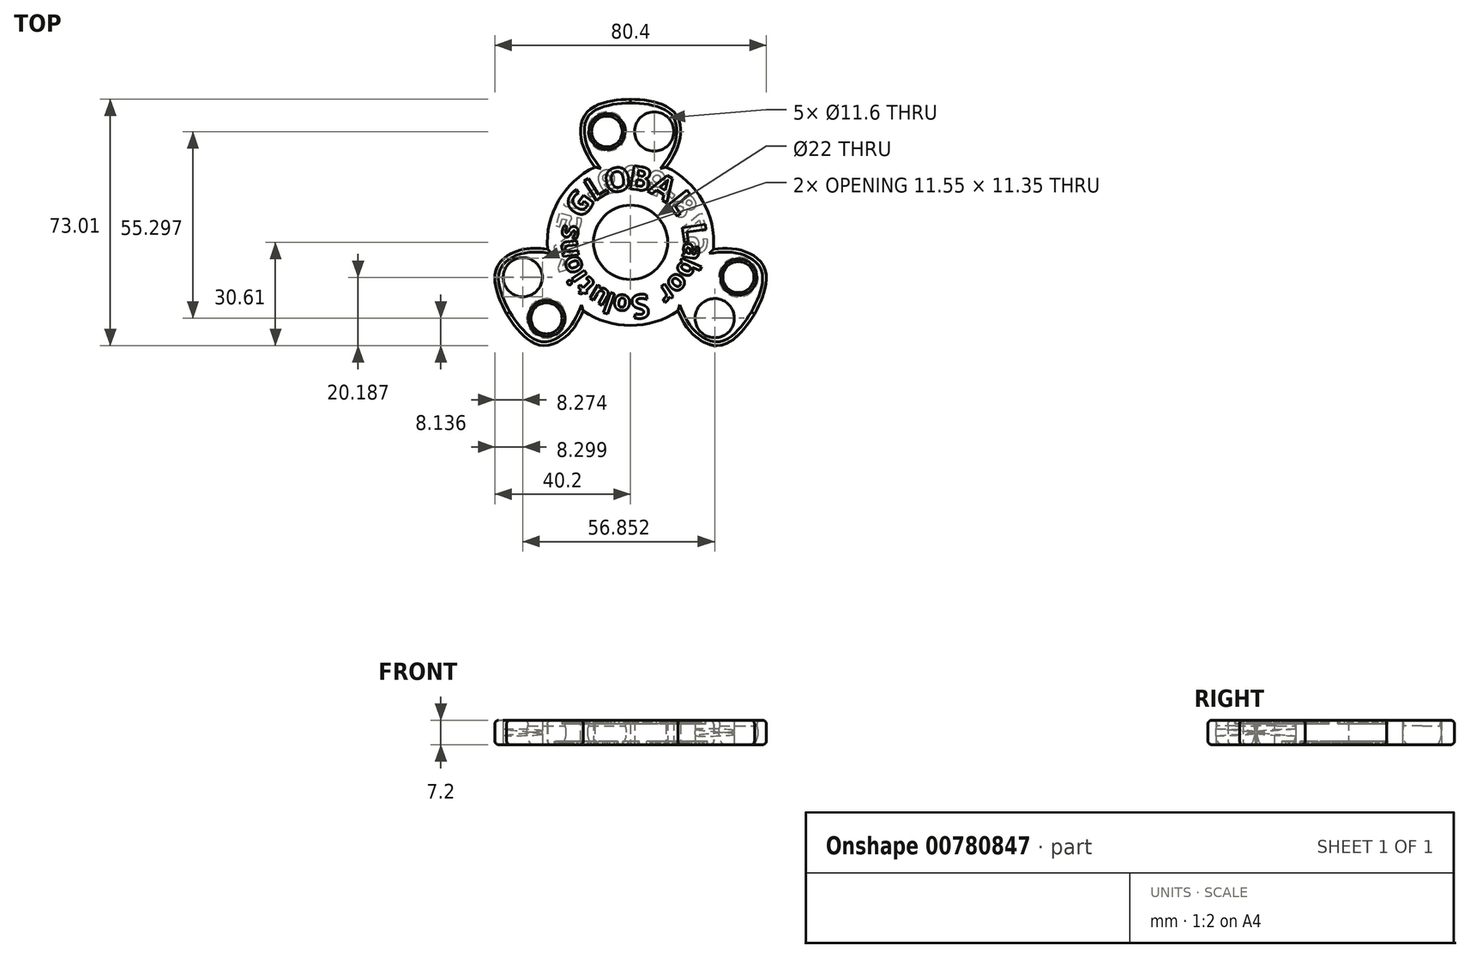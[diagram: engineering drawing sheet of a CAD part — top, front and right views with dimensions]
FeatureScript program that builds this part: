
annotation { "Feature Type Name" : "Feature", "Feature Type Description" : "" }
export const myFeature = defineFeature(function(context is Context, id is Id, definition is map)
    precondition{}
    {
        {
            var Q0;
            Q0=qCreatedBy(makeId("Top.planeOp"),FACE);
            var sketch = newSketch(context, id + "F0", { "sketchPlane" : qUnion([Q0])});
            skCircle(sketch, "E0", {"center": v(0, 0) * mm, "radius": 11 * mm});
            skLineSegment(sketch, "E1", {"start": v(-60.62, 35) * mm, "end": v(57.4, -33.14) * mm, "construction": true});
            skLineSegment(sketch, "E2.MirrorCS", {"start": v(-60.62, -35) * mm, "end": v(57.4, 33.14) * mm, "construction": true});
            skLineSegment(sketch, "E3", {"start": v(-61.07, 42.4) * mm, "end": v(58.93, 42.4) * mm, "construction": true});
            skFitSpline(sketch, "E4", {"points": [v(-10.53, 22.28) * mm, v(-14.78, 33.34) * mm, v(0, 42.4) * mm], "startDerivative": vector(-20.82, 27.32) * mm, "endDerivative": vector(68.91, 1.84) * mm});
            skCircle(sketch, "E5", {"center": v(-7, 32.82) * mm, "radius": 5.8 * mm});
            skFitSpline(sketch, "E6.MirrorCS", {"points": [v(10.53, 22.28) * mm, v(14.78, 33.34) * mm, v(0, 42.4) * mm], "startDerivative": vector(20.82, 27.32) * mm, "endDerivative": vector(-68.91, 1.84) * mm});
            skCircle(sketch, "E7.MirrorC", {"center": v(7, 32.82) * mm, "radius": 5.8 * mm});
            skFitSpline(sketch, "E8.MirrorCS", {"points": [v(24.56, -2.02) * mm, v(36.26, -3.87) * mm, v(36.72, -21.2) * mm], "startDerivative": vector(34.07, 4.37) * mm, "endDerivative": vector(-32.86, -60.6) * mm});
            skFitSpline(sketch, "E9.MirrorCS", {"points": [v(14.03, -20.26) * mm, v(21.48, -29.47) * mm, v(36.72, -21.2) * mm], "startDerivative": vector(13.25, -31.7) * mm, "endDerivative": vector(36.05, 58.76) * mm});
            skCircle(sketch, "E10.MirrorC", {"center": v(24.93, -22.47) * mm, "radius": 5.8 * mm});
            skCircle(sketch, "E11.MirrorC", {"center": v(31.93, -10.35) * mm, "radius": 5.8 * mm});
            skFitSpline(sketch, "E12.MirrorCS", {"points": [v(-14.03, -20.26) * mm, v(-21.48, -29.47) * mm, v(-36.72, -21.2) * mm], "startDerivative": vector(-13.25, -31.7) * mm, "endDerivative": vector(-36.05, 58.76) * mm});
            skFitSpline(sketch, "E13.MirrorCS", {"points": [v(-24.56, -2.02) * mm, v(-36.26, -3.87) * mm, v(-36.72, -21.2) * mm], "startDerivative": vector(-34.07, 4.37) * mm, "endDerivative": vector(32.86, -60.6) * mm});
            skCircle(sketch, "E14.MirrorC", {"center": v(-31.93, -10.35) * mm, "radius": 5.8 * mm});
            skCircle(sketch, "E15.MirrorC", {"center": v(-24.93, -22.47) * mm, "radius": 5.8 * mm});
            skArc(sketch, "E16", {"start": v(-14.03, -20.26) * mm, "mid": v(0, -24.65) * mm, "end": v(14.03, -20.26) * mm});
            skArc(sketch, "E17.trimOffspring", {"start": v(-10.53, 22.28) * mm, "mid": v(-21.34, 12.32) * mm, "end": v(-24.56, -2.02) * mm});
            skArc(sketch, "E18.trimOffspring", {"start": v(24.56, -2.02) * mm, "mid": v(21.34, 12.32) * mm, "end": v(10.53, 22.28) * mm});
            skSolve(sketch);
        }
        {
            var Q0;
            {var subQ0=sQuery(id+"F0.wireOp",EDGE,"c7664de7-02b4-4db1-8378-9aed48db6bc2");Q0=makeQuery(id+"F0.imprint","IMPRINT",FACE,{"disambiguationData":[TD([[makeQuery(id+"F0.imprint","IMPRINT",EDGE,{"derivedFrom":subQ0}),-1.0]])]});}
            var Q1;
            Q1=makeQuery(id+"F0.imprint","IMPRINT",FACE,{"disambiguationData":[TD([[makeQuery(id+"F0.imprint","IMPRINT",EDGE,{"derivedFrom":sQuery(id+"F0.wireOp",EDGE,"E5")}),1.0]])]});
            var Q2;
            Q2=makeQuery(id+"F0.imprint","IMPRINT",FACE,{"disambiguationData":[TD([[makeQuery(id+"F0.imprint","IMPRINT",EDGE,{"derivedFrom":sQuery(id+"F0.wireOp",EDGE,"E7.MirrorC")}),-1.0]])]});
            var Q3;
            {var subQ0=sQuery(id+"F0.wireOp",EDGE,"b568a12d-a18f-46d6-a3cd-37dfae46e10a0.MirrorCS");Q3=makeQuery(id+"F0.imprint","IMPRINT",FACE,{"disambiguationData":[TD([[makeQuery(id+"F0.imprint","IMPRINT",EDGE,{"derivedFrom":subQ0}),1.0]])]});}
            var Q4;
            Q4=makeQuery(id+"F0.imprint","IMPRINT",FACE,{"disambiguationData":[TD([[makeQuery(id+"F0.imprint","IMPRINT",EDGE,{"derivedFrom":sQuery(id+"F0.wireOp",EDGE,"E8.MirrorCS")}),-1.0]])]});
            var Q5;
            Q5=makeQuery(id+"F0.imprint","IMPRINT",FACE,{"disambiguationData":[TD([[makeQuery(id+"F0.imprint","IMPRINT",EDGE,{"derivedFrom":sQuery(id+"F0.wireOp",EDGE,"E0")}),-1.0]])]});
            var Q6;
            Q6=makeQuery(id+"F0.imprint","IMPRINT",FACE,{"disambiguationData":[TD([[makeQuery(id+"F0.imprint","IMPRINT",EDGE,{"derivedFrom":sQuery(id+"F0.wireOp",EDGE,"E15.MirrorC")}),1.0]])]});
            var Q7;
            Q7=makeQuery(id+"F0.imprint","IMPRINT",FACE,{"disambiguationData":[TD([[makeQuery(id+"F0.imprint","IMPRINT",EDGE,{"derivedFrom":sQuery(id+"F0.wireOp",EDGE,"E14.MirrorC")}),-1.0]])]});
            var Q8;
            Q8=makeQuery(id+"F0.imprint","IMPRINT",FACE,{"disambiguationData":[TD([[makeQuery(id+"F0.imprint","IMPRINT",EDGE,{"derivedFrom":sQuery(id+"F0.wireOp",EDGE,"E10.MirrorC")}),-1.0]])]});
            var Q9;
            Q9=makeQuery(id+"F0.imprint","IMPRINT",FACE,{"disambiguationData":[TD([[makeQuery(id+"F0.imprint","IMPRINT",EDGE,{"derivedFrom":sQuery(id+"F0.wireOp",EDGE,"E11.MirrorC")}),1.0]])]});
            var Q10;
            {var subQ1=sQuery(id+"F0.wireOp",EDGE,"E12.MirrorCS");Q10=makeQuery(id+"F0.imprint","IMPRINT",FACE,{"disambiguationData":[TD([[makeQuery(id+"F0.imprint","IMPRINT",EDGE,{"derivedFrom":subQ1}),-1.0]])]});}
            var Q11;
            {var subQ1=sQuery(id+"F0.wireOp",EDGE,"E4");Q11=makeQuery(id+"F0.imprint","IMPRINT",FACE,{"disambiguationData":[TD([[makeQuery(id+"F0.imprint","IMPRINT",EDGE,{"derivedFrom":subQ1}),-1.0]])]});}
            var Q12;
            {var subQ0=sQuery(id+"F0.wireOp",EDGE,"584b3a96-3070-4e52-8d9e-0a283c081f860.MirrorCS");var subQ5=sQuery(id+"F0.wireOp",EDGE,"E16");var subQ6=makeQuery(id+"F0.imprint","INTERSECT",VERTEX,{"derivedFrom":[subQ0,subQ5]});Q12=makeQuery(id+"F0.imprint","IMPRINT",FACE,{"disambiguationData":[TD([[makeQuery(id+"F0.imprint","IMPRINT",EDGE,{"disambiguationData":[TD([[subQ6,1.0]])],"derivedFrom":subQ5}),1.0]])]});}
            var Q13;
            {var subQ1=sQuery(id+"F0.wireOp",EDGE,"709621ff-4ad7-4bf4-bf4e-122474cc28010.MirrorCS");var subQ3=sQuery(id+"F0.wireOp",EDGE,"E16");var subQ4=makeQuery(id+"F0.imprint","INTERSECT",VERTEX,{"derivedFrom":[subQ1,subQ3]});Q13=makeQuery(id+"F0.imprint","IMPRINT",FACE,{"disambiguationData":[TD([[makeQuery(id+"F0.imprint","IMPRINT",EDGE,{"disambiguationData":[TD([[subQ4,1.0]])],"derivedFrom":subQ3}),1.0]])]});}
            var Q14;
            {var subQ1=sQuery(id+"F0.wireOp",EDGE,"c7664de7-02b4-4db1-8378-9aed48db6bc2");var subQ3=sQuery(id+"F0.wireOp",EDGE,"E16");var subQ4=makeQuery(id+"F0.imprint","INTERSECT",VERTEX,{"derivedFrom":[subQ1,subQ3]});Q14=makeQuery(id+"F0.imprint","IMPRINT",FACE,{"disambiguationData":[TD([[makeQuery(id+"F0.imprint","IMPRINT",EDGE,{"disambiguationData":[TD([[subQ4,-1.0]])],"derivedFrom":subQ3}),1.0]])]});}
            var Q15;
            {var subQ1=sQuery(id+"F0.wireOp",EDGE,"4d5f6e66-4a7b-47e1-8b82-9a1195048e960.MirrorCS");var subQ3=sQuery(id+"F0.wireOp",EDGE,"E16");var subQ4=makeQuery(id+"F0.imprint","INTERSECT",VERTEX,{"derivedFrom":[subQ1,subQ3]});Q15=makeQuery(id+"F0.imprint","IMPRINT",FACE,{"disambiguationData":[TD([[makeQuery(id+"F0.imprint","IMPRINT",EDGE,{"disambiguationData":[TD([[subQ4,1.0]])],"derivedFrom":subQ3}),1.0]])]});}
            extrude(context, id + "F1", {"entities" : qUnion([Q0, Q1, Q2, Q3, Q4, Q5, Q6, Q7, Q8, Q9, Q10, Q11, Q12, Q13, Q14, Q15]), "depth" : 7.2 * mm, "offsetDistance" : 25 * mm});
        }
        {
            var Q0;
            Q0=qCreatedBy(makeId("Top.planeOp"),FACE);
            cPlane(context, id + "F2", {"entities" : qUnion([Q0]), "cplaneType" : CPlaneType.OFFSET, "offset" : 3.6 * mm, "width" : 150 * mm, "height" : 150 * mm});
        }
        {
            var Q0;
            Q0=qCreatedBy(id+"F2.planeOp",FACE);
            var sketch = newSketch(context, id + "F3", { "sketchPlane" : qUnion([Q0])});
            skArc(sketch, "E19.0", {"start": v(-1.2, 32.82) * mm, "mid": v(-7, 38.62) * mm, "end": v(-12.8, 32.82) * mm});
            skArc(sketch, "E20.0", {"start": v(1.2, 32.82) * mm, "mid": v(7, 38.62) * mm, "end": v(12.8, 32.82) * mm});
            skLineSegment(sketch, "E21", {"start": v(-12.8, 32.82) * mm, "end": v(-1.2, 32.82) * mm});
            skLineSegment(sketch, "E22.MirrorCS", {"start": v(12.8, 32.82) * mm, "end": v(1.2, 32.82) * mm});
            skSolve(sketch);
        }
        {
            var Q0;
            Q0=qSketchRegion(id+"F3",true);
            var Q1;
            Q1=sQuery(id+"F3.wireOp",EDGE,"E21");
            revolve(context, id + "F4", {"operationType" : NewBodyOperationType.REMOVE, "surfaceOperationType" : NewSurfaceOperationType.NEW, "entities" : qUnion([Q0]), "axis" : qUnion([Q1]), "revolveType" : RevolveType.FULL, "oppositeDirection" : true});
        }
        {
            var Q0;
            Q0=qCreatedBy(id+"F2.planeOp",FACE);
            var sketch = newSketch(context, id + "F5", { "sketchPlane" : qUnion([Q0])});
            skLineSegment(sketch, "E23.MirrorCS", {"start": v(-34.88, -5.24) * mm, "end": v(-29.03, -15.37) * mm});
            skLineSegment(sketch, "E24.MirrorCS", {"start": v(-21.98, -27.58) * mm, "end": v(-27.83, -17.45) * mm});
            skArc(sketch, "E25.MirrorCS", {"start": v(-27.83, -17.45) * mm, "mid": v(-29.97, -25.44) * mm, "end": v(-21.98, -27.58) * mm});
            skArc(sketch, "E26.MirrorCS", {"start": v(-29.03, -15.37) * mm, "mid": v(-37.02, -13.23) * mm, "end": v(-34.88, -5.24) * mm});
            skSolve(sketch);
        }
        {
            var Q0;
            Q0=qSketchRegion(id+"F5",true);
            var Q1;
            Q1=sQuery(id+"F5.wireOp",EDGE,"E23.MirrorCS");
            revolve(context, id + "F6", {"operationType" : NewBodyOperationType.REMOVE, "surfaceOperationType" : NewSurfaceOperationType.NEW, "entities" : qUnion([Q0]), "axis" : qUnion([Q1]), "revolveType" : RevolveType.FULL, "oppositeDirection" : true});
        }
        {
            var Q0;
            Q0=qCreatedBy(id+"F2.planeOp",FACE);
            var sketch = newSketch(context, id + "F7", { "sketchPlane" : qUnion([Q0])});
            skLineSegment(sketch, "E27.MirrorCS", {"start": v(34.88, -5.24) * mm, "end": v(29.03, -15.37) * mm});
            skLineSegment(sketch, "E28.MirrorCS", {"start": v(21.98, -27.58) * mm, "end": v(27.83, -17.45) * mm});
            skArc(sketch, "E29.MirrorCS", {"start": v(27.83, -17.45) * mm, "mid": v(29.97, -25.44) * mm, "end": v(21.98, -27.58) * mm});
            skArc(sketch, "E30.MirrorCS", {"start": v(29.03, -15.37) * mm, "mid": v(37.02, -13.23) * mm, "end": v(34.88, -5.24) * mm});
            skSolve(sketch);
        }
        {
            var Q0;
            Q0=qSketchRegion(id+"F7",true);
            var Q1;
            Q1=sQuery(id+"F7.wireOp",EDGE,"E28.MirrorCS");
            revolve(context, id + "F8", {"operationType" : NewBodyOperationType.REMOVE, "surfaceOperationType" : NewSurfaceOperationType.NEW, "entities" : qUnion([Q0]), "axis" : qUnion([Q1]), "revolveType" : RevolveType.FULL, "oppositeDirection" : true});
        }
        {
            var Q0;
            Q0=makeQuery(id+"F4.boolean.opBoolean","INTERSECT",EDGE,{"derivedFrom":[makeQuery(id+"F1.opExtrude","CAP_FACE",FACE,{"disambiguationData":[OSD([sQuery(id+"F0.wireOp",EDGE,"E0"),sQuery(id+"F0.wireOp",EDGE,"c7664de7-02b4-4db1-8378-9aed48db6bc2"),sQuery(id+"F0.wireOp",EDGE,"E4"),sQuery(id+"F0.wireOp",EDGE,"E6.MirrorCS"),sQuery(id+"F0.wireOp",EDGE,"709621ff-4ad7-4bf4-bf4e-122474cc28010.MirrorCS"),sQuery(id+"F0.wireOp",EDGE,"E8.MirrorCS"),sQuery(id+"F0.wireOp",EDGE,"584b3a96-3070-4e52-8d9e-0a283c081f860.MirrorCS"),sQuery(id+"F0.wireOp",EDGE,"E9.MirrorCS"),sQuery(id+"F0.wireOp",EDGE,"4d5f6e66-4a7b-47e1-8b82-9a1195048e960.MirrorCS"),sQuery(id+"F0.wireOp",EDGE,"b568a12d-a18f-46d6-a3cd-37dfae46e10a0.MirrorCS"),sQuery(id+"F0.wireOp",EDGE,"806fca16-4be0-40c0-a4df-1d6eb79cdd150.MirrorCS"),sQuery(id+"F0.wireOp",EDGE,"E12.MirrorCS"),sQuery(id+"F0.wireOp",EDGE,"E13.MirrorCS")])],"isStart":false}),makeQuery(id+"F4.opRevolve","SWEPT_FACE",FACE,{"disambiguationData":[OSD([sQuery(id+"F3.wireOp",EDGE,"E19.0")])]})]});
            var Q1;
            Q1=makeQuery(id+"F4.boolean.opBoolean","INTERSECT",EDGE,{"derivedFrom":[makeQuery(id+"F1.opExtrude","CAP_FACE",FACE,{"disambiguationData":[OSD([sQuery(id+"F0.wireOp",EDGE,"E0"),sQuery(id+"F0.wireOp",EDGE,"c7664de7-02b4-4db1-8378-9aed48db6bc2"),sQuery(id+"F0.wireOp",EDGE,"E4"),sQuery(id+"F0.wireOp",EDGE,"E6.MirrorCS"),sQuery(id+"F0.wireOp",EDGE,"709621ff-4ad7-4bf4-bf4e-122474cc28010.MirrorCS"),sQuery(id+"F0.wireOp",EDGE,"E8.MirrorCS"),sQuery(id+"F0.wireOp",EDGE,"584b3a96-3070-4e52-8d9e-0a283c081f860.MirrorCS"),sQuery(id+"F0.wireOp",EDGE,"E9.MirrorCS"),sQuery(id+"F0.wireOp",EDGE,"4d5f6e66-4a7b-47e1-8b82-9a1195048e960.MirrorCS"),sQuery(id+"F0.wireOp",EDGE,"b568a12d-a18f-46d6-a3cd-37dfae46e10a0.MirrorCS"),sQuery(id+"F0.wireOp",EDGE,"806fca16-4be0-40c0-a4df-1d6eb79cdd150.MirrorCS"),sQuery(id+"F0.wireOp",EDGE,"E12.MirrorCS"),sQuery(id+"F0.wireOp",EDGE,"E13.MirrorCS")])],"isStart":false}),makeQuery(id+"F4.opRevolve","SWEPT_FACE",FACE,{"disambiguationData":[OSD([sQuery(id+"F3.wireOp",EDGE,"E20.0")])]})]});
            var Q2;
            Q2=makeQuery(id+"F8.boolean.opBoolean","INTERSECT",EDGE,{"derivedFrom":[makeQuery(id+"F1.opExtrude","CAP_FACE",FACE,{"disambiguationData":[OSD([sQuery(id+"F0.wireOp",EDGE,"E0"),sQuery(id+"F0.wireOp",EDGE,"c7664de7-02b4-4db1-8378-9aed48db6bc2"),sQuery(id+"F0.wireOp",EDGE,"E4"),sQuery(id+"F0.wireOp",EDGE,"E6.MirrorCS"),sQuery(id+"F0.wireOp",EDGE,"709621ff-4ad7-4bf4-bf4e-122474cc28010.MirrorCS"),sQuery(id+"F0.wireOp",EDGE,"E8.MirrorCS"),sQuery(id+"F0.wireOp",EDGE,"584b3a96-3070-4e52-8d9e-0a283c081f860.MirrorCS"),sQuery(id+"F0.wireOp",EDGE,"E9.MirrorCS"),sQuery(id+"F0.wireOp",EDGE,"4d5f6e66-4a7b-47e1-8b82-9a1195048e960.MirrorCS"),sQuery(id+"F0.wireOp",EDGE,"b568a12d-a18f-46d6-a3cd-37dfae46e10a0.MirrorCS"),sQuery(id+"F0.wireOp",EDGE,"806fca16-4be0-40c0-a4df-1d6eb79cdd150.MirrorCS"),sQuery(id+"F0.wireOp",EDGE,"E12.MirrorCS"),sQuery(id+"F0.wireOp",EDGE,"E13.MirrorCS")])],"isStart":false}),makeQuery(id+"F8.opRevolve","SWEPT_FACE",FACE,{"disambiguationData":[OSD([sQuery(id+"F7.wireOp",EDGE,"E30.MirrorCS")])]})]});
            var Q3;
            Q3=makeQuery(id+"F8.boolean.opBoolean","INTERSECT",EDGE,{"derivedFrom":[makeQuery(id+"F1.opExtrude","CAP_FACE",FACE,{"disambiguationData":[OSD([sQuery(id+"F0.wireOp",EDGE,"E0"),sQuery(id+"F0.wireOp",EDGE,"c7664de7-02b4-4db1-8378-9aed48db6bc2"),sQuery(id+"F0.wireOp",EDGE,"E4"),sQuery(id+"F0.wireOp",EDGE,"E6.MirrorCS"),sQuery(id+"F0.wireOp",EDGE,"709621ff-4ad7-4bf4-bf4e-122474cc28010.MirrorCS"),sQuery(id+"F0.wireOp",EDGE,"E8.MirrorCS"),sQuery(id+"F0.wireOp",EDGE,"584b3a96-3070-4e52-8d9e-0a283c081f860.MirrorCS"),sQuery(id+"F0.wireOp",EDGE,"E9.MirrorCS"),sQuery(id+"F0.wireOp",EDGE,"4d5f6e66-4a7b-47e1-8b82-9a1195048e960.MirrorCS"),sQuery(id+"F0.wireOp",EDGE,"b568a12d-a18f-46d6-a3cd-37dfae46e10a0.MirrorCS"),sQuery(id+"F0.wireOp",EDGE,"806fca16-4be0-40c0-a4df-1d6eb79cdd150.MirrorCS"),sQuery(id+"F0.wireOp",EDGE,"E12.MirrorCS"),sQuery(id+"F0.wireOp",EDGE,"E13.MirrorCS")])],"isStart":false}),makeQuery(id+"F8.opRevolve","SWEPT_FACE",FACE,{"disambiguationData":[OSD([sQuery(id+"F7.wireOp",EDGE,"E29.MirrorCS")])]})]});
            var Q4;
            Q4=makeQuery(id+"F6.boolean.opBoolean","INTERSECT",EDGE,{"derivedFrom":[makeQuery(id+"F1.opExtrude","CAP_FACE",FACE,{"disambiguationData":[OSD([sQuery(id+"F0.wireOp",EDGE,"E0"),sQuery(id+"F0.wireOp",EDGE,"c7664de7-02b4-4db1-8378-9aed48db6bc2"),sQuery(id+"F0.wireOp",EDGE,"E4"),sQuery(id+"F0.wireOp",EDGE,"E6.MirrorCS"),sQuery(id+"F0.wireOp",EDGE,"709621ff-4ad7-4bf4-bf4e-122474cc28010.MirrorCS"),sQuery(id+"F0.wireOp",EDGE,"E8.MirrorCS"),sQuery(id+"F0.wireOp",EDGE,"584b3a96-3070-4e52-8d9e-0a283c081f860.MirrorCS"),sQuery(id+"F0.wireOp",EDGE,"E9.MirrorCS"),sQuery(id+"F0.wireOp",EDGE,"4d5f6e66-4a7b-47e1-8b82-9a1195048e960.MirrorCS"),sQuery(id+"F0.wireOp",EDGE,"b568a12d-a18f-46d6-a3cd-37dfae46e10a0.MirrorCS"),sQuery(id+"F0.wireOp",EDGE,"806fca16-4be0-40c0-a4df-1d6eb79cdd150.MirrorCS"),sQuery(id+"F0.wireOp",EDGE,"E12.MirrorCS"),sQuery(id+"F0.wireOp",EDGE,"E13.MirrorCS")])],"isStart":false}),makeQuery(id+"F6.opRevolve","SWEPT_FACE",FACE,{"disambiguationData":[OSD([sQuery(id+"F5.wireOp",EDGE,"E25.MirrorCS")])]})]});
            var Q5;
            Q5=makeQuery(id+"F6.boolean.opBoolean","INTERSECT",EDGE,{"derivedFrom":[makeQuery(id+"F1.opExtrude","CAP_FACE",FACE,{"disambiguationData":[OSD([sQuery(id+"F0.wireOp",EDGE,"E0"),sQuery(id+"F0.wireOp",EDGE,"c7664de7-02b4-4db1-8378-9aed48db6bc2"),sQuery(id+"F0.wireOp",EDGE,"E4"),sQuery(id+"F0.wireOp",EDGE,"E6.MirrorCS"),sQuery(id+"F0.wireOp",EDGE,"709621ff-4ad7-4bf4-bf4e-122474cc28010.MirrorCS"),sQuery(id+"F0.wireOp",EDGE,"E8.MirrorCS"),sQuery(id+"F0.wireOp",EDGE,"584b3a96-3070-4e52-8d9e-0a283c081f860.MirrorCS"),sQuery(id+"F0.wireOp",EDGE,"E9.MirrorCS"),sQuery(id+"F0.wireOp",EDGE,"4d5f6e66-4a7b-47e1-8b82-9a1195048e960.MirrorCS"),sQuery(id+"F0.wireOp",EDGE,"b568a12d-a18f-46d6-a3cd-37dfae46e10a0.MirrorCS"),sQuery(id+"F0.wireOp",EDGE,"806fca16-4be0-40c0-a4df-1d6eb79cdd150.MirrorCS"),sQuery(id+"F0.wireOp",EDGE,"E12.MirrorCS"),sQuery(id+"F0.wireOp",EDGE,"E13.MirrorCS")])],"isStart":false}),makeQuery(id+"F6.opRevolve","SWEPT_FACE",FACE,{"disambiguationData":[OSD([sQuery(id+"F5.wireOp",EDGE,"E26.MirrorCS")])]})]});
            fillet(context, id + "F9", {"entities" : qUnion([Q0, Q1, Q2, Q3, Q4, Q5]), "radius" : 1.2 * mm, "tangentPropagation" : true, "allowEdgeOverflow" : false});
        }
        {
            var Q0;
            Q0=makeQuery(id+"F1.opExtrude","CAP_EDGE",EDGE,{"disambiguationData":[OSD([sQuery(id+"F0.wireOp",EDGE,"E4")])],"isStart":false});
            var Q1;
            Q1=makeQuery(id+"F1.opExtrude","CAP_EDGE",EDGE,{"disambiguationData":[OSD([sQuery(id+"F0.wireOp",EDGE,"c7664de7-02b4-4db1-8378-9aed48db6bc2")])],"isStart":false});
            var Q2;
            Q2=makeQuery(id+"F1.opExtrude","CAP_EDGE",EDGE,{"disambiguationData":[OSD([sQuery(id+"F0.wireOp",EDGE,"E6.MirrorCS")])],"isStart":false});
            var Q3;
            Q3=makeQuery(id+"F1.opExtrude","CAP_EDGE",EDGE,{"disambiguationData":[OSD([sQuery(id+"F0.wireOp",EDGE,"709621ff-4ad7-4bf4-bf4e-122474cc28010.MirrorCS")])],"isStart":false});
            var Q4;
            Q4=makeQuery(id+"F1.opExtrude","CAP_EDGE",EDGE,{"disambiguationData":[OSD([sQuery(id+"F0.wireOp",EDGE,"c7664de7-02b4-4db1-8378-9aed48db6bc2")])],"isStart":true});
            var Q5;
            Q5=makeQuery(id+"F1.opExtrude","CAP_EDGE",EDGE,{"disambiguationData":[OSD([sQuery(id+"F0.wireOp",EDGE,"709621ff-4ad7-4bf4-bf4e-122474cc28010.MirrorCS")])],"isStart":true});
            var Q6;
            Q6=makeQuery(id+"F1.opExtrude","CAP_EDGE",EDGE,{"disambiguationData":[OSD([sQuery(id+"F0.wireOp",EDGE,"E6.MirrorCS")])],"isStart":true});
            var Q7;
            Q7=makeQuery(id+"F1.opExtrude","CAP_EDGE",EDGE,{"disambiguationData":[OSD([sQuery(id+"F0.wireOp",EDGE,"E4")])],"isStart":true});
            var Q8;
            Q8=makeQuery(id+"F1.opExtrude","CAP_EDGE",EDGE,{"disambiguationData":[OSD([sQuery(id+"F0.wireOp",EDGE,"b568a12d-a18f-46d6-a3cd-37dfae46e10a0.MirrorCS")])],"isStart":false});
            var Q9;
            Q9=makeQuery(id+"F1.opExtrude","CAP_EDGE",EDGE,{"disambiguationData":[OSD([sQuery(id+"F0.wireOp",EDGE,"E13.MirrorCS")])],"isStart":false});
            var Q10;
            Q10=makeQuery(id+"F1.opExtrude","CAP_EDGE",EDGE,{"disambiguationData":[OSD([sQuery(id+"F0.wireOp",EDGE,"E12.MirrorCS")])],"isStart":false});
            var Q11;
            Q11=makeQuery(id+"F1.opExtrude","CAP_EDGE",EDGE,{"disambiguationData":[OSD([sQuery(id+"F0.wireOp",EDGE,"806fca16-4be0-40c0-a4df-1d6eb79cdd150.MirrorCS")])],"isStart":false});
            var Q12;
            Q12=makeQuery(id+"F1.opExtrude","CAP_EDGE",EDGE,{"disambiguationData":[OSD([sQuery(id+"F0.wireOp",EDGE,"4d5f6e66-4a7b-47e1-8b82-9a1195048e960.MirrorCS")])],"isStart":false});
            var Q13;
            Q13=makeQuery(id+"F1.opExtrude","CAP_EDGE",EDGE,{"disambiguationData":[OSD([sQuery(id+"F0.wireOp",EDGE,"E9.MirrorCS")])],"isStart":false});
            var Q14;
            Q14=makeQuery(id+"F1.opExtrude","CAP_EDGE",EDGE,{"disambiguationData":[OSD([sQuery(id+"F0.wireOp",EDGE,"E8.MirrorCS")])],"isStart":false});
            var Q15;
            Q15=makeQuery(id+"F1.opExtrude","CAP_EDGE",EDGE,{"disambiguationData":[OSD([sQuery(id+"F0.wireOp",EDGE,"584b3a96-3070-4e52-8d9e-0a283c081f860.MirrorCS")])],"isStart":false});
            var Q16;
            Q16=makeQuery(id+"F1.opExtrude","CAP_EDGE",EDGE,{"disambiguationData":[OSD([sQuery(id+"F0.wireOp",EDGE,"584b3a96-3070-4e52-8d9e-0a283c081f860.MirrorCS")])],"isStart":true});
            var Q17;
            Q17=makeQuery(id+"F1.opExtrude","CAP_EDGE",EDGE,{"disambiguationData":[OSD([sQuery(id+"F0.wireOp",EDGE,"b568a12d-a18f-46d6-a3cd-37dfae46e10a0.MirrorCS")])],"isStart":true});
            var Q18;
            Q18=makeQuery(id+"F1.opExtrude","CAP_EDGE",EDGE,{"disambiguationData":[OSD([sQuery(id+"F0.wireOp",EDGE,"E13.MirrorCS")])],"isStart":true});
            var Q19;
            Q19=makeQuery(id+"F1.opExtrude","CAP_EDGE",EDGE,{"disambiguationData":[OSD([sQuery(id+"F0.wireOp",EDGE,"E12.MirrorCS")])],"isStart":true});
            var Q20;
            Q20=makeQuery(id+"F1.opExtrude","CAP_EDGE",EDGE,{"disambiguationData":[OSD([sQuery(id+"F0.wireOp",EDGE,"806fca16-4be0-40c0-a4df-1d6eb79cdd150.MirrorCS")])],"isStart":true});
            var Q21;
            Q21=makeQuery(id+"F1.opExtrude","CAP_EDGE",EDGE,{"disambiguationData":[OSD([sQuery(id+"F0.wireOp",EDGE,"4d5f6e66-4a7b-47e1-8b82-9a1195048e960.MirrorCS")])],"isStart":true});
            var Q22;
            Q22=makeQuery(id+"F1.opExtrude","CAP_EDGE",EDGE,{"disambiguationData":[OSD([sQuery(id+"F0.wireOp",EDGE,"E9.MirrorCS")])],"isStart":true});
            var Q23;
            Q23=makeQuery(id+"F1.opExtrude","CAP_EDGE",EDGE,{"disambiguationData":[OSD([sQuery(id+"F0.wireOp",EDGE,"E8.MirrorCS")])],"isStart":true});
            var Q24;
            {var subQ0=sQuery(id+"F0.wireOp",EDGE,"E16");Q24=makeQuery(id+"F1.opExtrude","CAP_EDGE",EDGE,{"disambiguationData":[OSD([subQ0]),TDD([makeQuery(id+"F0.imprint","IMPRINT",EDGE,{"disambiguationData":[TD([[makeQuery(id+"F0.imprint","INTERSECT",VERTEX,{"derivedFrom":[sQuery(id+"F0.wireOp",EDGE,"c7664de7-02b4-4db1-8378-9aed48db6bc2"),subQ0]}),-1.0]])],"derivedFrom":subQ0})])],"isStart":false});}
            var Q25;
            {var subQ0=sQuery(id+"F0.wireOp",EDGE,"E16");Q25=makeQuery(id+"F1.opExtrude","CAP_EDGE",EDGE,{"disambiguationData":[OSD([subQ0]),TDD([makeQuery(id+"F0.imprint","IMPRINT",EDGE,{"disambiguationData":[TD([[makeQuery(id+"F0.imprint","INTERSECT",VERTEX,{"derivedFrom":[sQuery(id+"F0.wireOp",EDGE,"709621ff-4ad7-4bf4-bf4e-122474cc28010.MirrorCS"),subQ0]}),1.0]])],"derivedFrom":subQ0})])],"isStart":false});}
            var Q26;
            {var subQ0=sQuery(id+"F0.wireOp",EDGE,"E16");Q26=makeQuery(id+"F1.opExtrude","CAP_EDGE",EDGE,{"disambiguationData":[OSD([subQ0]),TDD([makeQuery(id+"F0.imprint","IMPRINT",EDGE,{"disambiguationData":[TD([[makeQuery(id+"F0.imprint","INTERSECT",VERTEX,{"derivedFrom":[sQuery(id+"F0.wireOp",EDGE,"4d5f6e66-4a7b-47e1-8b82-9a1195048e960.MirrorCS"),subQ0]}),1.0]])],"derivedFrom":subQ0})])],"isStart":false});}
            var Q27;
            {var subQ0=sQuery(id+"F0.wireOp",EDGE,"E16");Q27=makeQuery(id+"F1.opExtrude","CAP_EDGE",EDGE,{"disambiguationData":[OSD([subQ0]),TDD([makeQuery(id+"F0.imprint","IMPRINT",EDGE,{"disambiguationData":[TD([[makeQuery(id+"F0.imprint","INTERSECT",VERTEX,{"derivedFrom":[sQuery(id+"F0.wireOp",EDGE,"c7664de7-02b4-4db1-8378-9aed48db6bc2"),subQ0]}),-1.0]])],"derivedFrom":subQ0})])],"isStart":true});}
            var Q28;
            {var subQ0=sQuery(id+"F0.wireOp",EDGE,"E16");Q28=makeQuery(id+"F1.opExtrude","CAP_EDGE",EDGE,{"disambiguationData":[OSD([subQ0]),TDD([makeQuery(id+"F0.imprint","IMPRINT",EDGE,{"disambiguationData":[TD([[makeQuery(id+"F0.imprint","INTERSECT",VERTEX,{"derivedFrom":[sQuery(id+"F0.wireOp",EDGE,"709621ff-4ad7-4bf4-bf4e-122474cc28010.MirrorCS"),subQ0]}),1.0]])],"derivedFrom":subQ0})])],"isStart":true});}
            var Q29;
            {var subQ0=sQuery(id+"F0.wireOp",EDGE,"E16");Q29=makeQuery(id+"F1.opExtrude","CAP_EDGE",EDGE,{"disambiguationData":[OSD([subQ0]),TDD([makeQuery(id+"F0.imprint","IMPRINT",EDGE,{"disambiguationData":[TD([[makeQuery(id+"F0.imprint","INTERSECT",VERTEX,{"derivedFrom":[sQuery(id+"F0.wireOp",EDGE,"4d5f6e66-4a7b-47e1-8b82-9a1195048e960.MirrorCS"),subQ0]}),1.0]])],"derivedFrom":subQ0})])],"isStart":true});}
            var Q30;
            Q30=makeQuery(id+"F1.opExtrude","CAP_EDGE",EDGE,{"disambiguationData":[OSD([sQuery(id+"F0.wireOp",EDGE,"E17.trimOffspring")])],"isStart":false});
            var Q31;
            Q31=makeQuery(id+"F1.opExtrude","CAP_EDGE",EDGE,{"disambiguationData":[OSD([sQuery(id+"F0.wireOp",EDGE,"E17.trimOffspring")])],"isStart":true});
            var Q32;
            Q32=makeQuery(id+"F1.opExtrude","CAP_EDGE",EDGE,{"disambiguationData":[OSD([sQuery(id+"F0.wireOp",EDGE,"E18.trimOffspring")])],"isStart":false});
            var Q33;
            Q33=makeQuery(id+"F1.opExtrude","CAP_EDGE",EDGE,{"disambiguationData":[OSD([sQuery(id+"F0.wireOp",EDGE,"E18.trimOffspring")])],"isStart":true});
            fillet(context, id + "F10", {"entities" : qUnion([Q0, Q1, Q2, Q3, Q4, Q5, Q6, Q7, Q8, Q9, Q10, Q11, Q12, Q13, Q14, Q15, Q16, Q17, Q18, Q19, Q20, Q21, Q22, Q23, Q24, Q25, Q26, Q27, Q28, Q29, Q30, Q31, Q32, Q33]), "radius" : 1.1 * mm, "tangentPropagation" : true, "allowEdgeOverflow" : false});
        }
        {
            var Q0;
            Q0=makeQuery(id+"F1.opExtrude","CAP_FACE",FACE,{"disambiguationData":[OSD([sQuery(id+"F0.wireOp",EDGE,"E0"),sQuery(id+"F0.wireOp",EDGE,"E4"),sQuery(id+"F0.wireOp",EDGE,"E6.MirrorCS"),sQuery(id+"F0.wireOp",EDGE,"E8.MirrorCS"),sQuery(id+"F0.wireOp",EDGE,"E9.MirrorCS"),sQuery(id+"F0.wireOp",EDGE,"E12.MirrorCS"),sQuery(id+"F0.wireOp",EDGE,"E13.MirrorCS"),sQuery(id+"F0.wireOp",EDGE,"E16"),sQuery(id+"F0.wireOp",EDGE,"E17.trimOffspring"),sQuery(id+"F0.wireOp",EDGE,"E18.trimOffspring")])],"isStart":false});
            var sketch = newSketch(context, id + "F11", { "sketchPlane" : qUnion([Q0])});
            skCircle(sketch, "E31", {"center": v(0, 0) * mm, "radius": 11 * mm});
            skCircle(sketch, "E32", {"center": v(0, 0) * mm, "radius": 16 * mm});
            skText(sketch, "E33", { "text": "G", "fontName": "OpenSans-Bold.ttf"});
            skText(sketch, "E34", { "text": "L", "fontName": "OpenSans-Bold.ttf"});
            skText(sketch, "E35", { "text": "O", "fontName": "OpenSans-Bold.ttf"});
            skText(sketch, "E36", { "text": "B", "fontName": "OpenSans-Bold.ttf"});
            skText(sketch, "E37", { "text": "A", "fontName": "OpenSans-Bold.ttf"});
            skText(sketch, "E38", { "text": "L", "fontName": "OpenSans-Bold.ttf"});
            skText(sketch, "E39", { "text": "L", "fontName": "OpenSans-Bold.ttf"});
            skText(sketch, "E40", { "text": "a", "fontName": "OpenSans-Bold.ttf"});
            skText(sketch, "E41", { "text": "b", "fontName": "OpenSans-Bold.ttf"});
            skText(sketch, "E42", { "text": "o", "fontName": "OpenSans-Bold.ttf"});
            skText(sketch, "E43", { "text": "r", "fontName": "OpenSans-Bold.ttf"});
            skText(sketch, "E44", { "text": "S", "fontName": "OpenSans-Bold.ttf"});
            skText(sketch, "E45", { "text": "o", "fontName": "OpenSans-Bold.ttf"});
            skText(sketch, "E46", { "text": "l", "fontName": "OpenSans-Bold.ttf"});
            skText(sketch, "E47", { "text": "u", "fontName": "OpenSans-Bold.ttf"});
            skText(sketch, "E48", { "text": "t", "fontName": "OpenSans-Bold.ttf"});
            skText(sketch, "E49", { "text": "i", "fontName": "OpenSans-Bold.ttf"});
            skText(sketch, "E50", { "text": "o", "fontName": "OpenSans-Bold.ttf"});
            skText(sketch, "E51", { "text": "n", "fontName": "OpenSans-Bold.ttf"});
            skText(sketch, "E52", { "text": "s", "fontName": "OpenSans-Bold.ttf"});
            const initialGuessF11  = {"E33": [-0.01454, 0.00668, 0.60363, 0.79726, 0.007], "E34": [-0.01081, 0.0118, 0.8472, 0.53126, 0.007], "E35": [-0.00697, 0.0144, 0.97925, 0.20264, 0.007], "E36": [-0.00087, 0.01598, 0.98803, -0.15426, 0.007], "E37": [0.00508, 0.01517, 0.85017, -0.5265, 0.007], "E38": [0.01515, 0.00515, 0.14512, -0.98941, 0.007], "E39": [0.0107, 0.01189, 0.60961, -0.7927, 0.007], "E40": [0.016, 0.0001, -0.1484, -0.98893, 0.006], "E41": [0.01548, -0.00405, -0.4138, -0.91037, 0.006], "E42": [0.0136, -0.00843, -0.6612, -0.75021, 0.006], "E43": [0.01062, -0.01197, -0.82786, -0.56094, 0.006], "E44": [0.00507, -0.01517, -0.98924, -0.1463, 0.007], "E45": [0.00036, -0.016, -0.98959, 0.14395, 0.006], "E46": [-0.00413, -0.01546, -0.94379, 0.33056, 0.006], "E47": [-0.00558, -0.015, -0.86545, 0.501, 0.006], "E48": [-0.01004, -0.01246, -0.6965, 0.71756, 0.006], "E49": [-0.01262, -0.00984, -0.55184, 0.83395, 0.006], "E50": [-0.01378, -0.00814, -0.35813, 0.93367, 0.006], "E51": [-0.0154, -0.00434, -0.10518, 0.99445, 0.006], "E52": [-0.01599, 0.00064, 0.17578, 0.98443, 0.006]};
            skSetInitialGuess(sketch, initialGuessF11);
            skSolve(sketch);
        }
        {
            var Q0;
            Q0=makeQuery(id+"F11.imprint","IMPRINT",FACE,{"disambiguationData":[TD([[makeQuery(id+"F11.imprint","IMPRINT",EDGE,{"derivedFrom":sQuery(id+"F11.wireOp",EDGE,"E33.sketch_text.stroke-0")}),-1.0]])]});
            var Q1;
            {var subQ0=sQuery(id+"F11.wireOp",EDGE,"E34.sketch_text.stroke-1");Q1=makeQuery(id+"F11.imprint","IMPRINT",FACE,{"disambiguationData":[TD([[makeQuery(id+"F11.imprint","IMPRINT",EDGE,{"derivedFrom":subQ0}),-1.0]])]});}
            var Q2;
            {var subQ6=sQuery(id+"F11.wireOp",EDGE,"E35.sketch_text.stroke-0");Q2=makeQuery(id+"F11.imprint","IMPRINT",FACE,{"disambiguationData":[TD([[makeQuery(id+"F11.imprint","IMPRINT",EDGE,{"derivedFrom":subQ6}),-1.0]])]});}
            var Q3;
            {var subQ6=sQuery(id+"F11.wireOp",EDGE,"E36.sketch_text.stroke-0");Q3=makeQuery(id+"F11.imprint","IMPRINT",FACE,{"disambiguationData":[TD([[makeQuery(id+"F11.imprint","IMPRINT",EDGE,{"derivedFrom":subQ6}),-1.0]])]});}
            var Q4;
            {var subQ7=sQuery(id+"F11.wireOp",EDGE,"E37.sketch_text.stroke-1");Q4=makeQuery(id+"F11.imprint","IMPRINT",FACE,{"disambiguationData":[TD([[makeQuery(id+"F11.imprint","IMPRINT",EDGE,{"derivedFrom":subQ7}),-1.0]])]});}
            var Q5;
            {var subQ0=sQuery(id+"F11.wireOp",EDGE,"E38.sketch_text.stroke-1");Q5=makeQuery(id+"F11.imprint","IMPRINT",FACE,{"disambiguationData":[TD([[makeQuery(id+"F11.imprint","IMPRINT",EDGE,{"derivedFrom":subQ0}),-1.0]])]});}
            var Q6;
            {var subQ0=sQuery(id+"F11.wireOp",EDGE,"E39.sketch_text.stroke-1");Q6=makeQuery(id+"F11.imprint","IMPRINT",FACE,{"disambiguationData":[TD([[makeQuery(id+"F11.imprint","IMPRINT",EDGE,{"derivedFrom":subQ0}),-1.0]])]});}
            var Q7;
            {var subQ4=sQuery(id+"F11.wireOp",EDGE,"E40.sketch_text.stroke-1");Q7=makeQuery(id+"F11.imprint","IMPRINT",FACE,{"disambiguationData":[TD([[makeQuery(id+"F11.imprint","IMPRINT",EDGE,{"derivedFrom":subQ4}),-1.0]])]});}
            var Q8;
            Q8=makeQuery(id+"F11.imprint","IMPRINT",FACE,{"disambiguationData":[TD([[makeQuery(id+"F11.imprint","IMPRINT",EDGE,{"derivedFrom":sQuery(id+"F11.wireOp",EDGE,"E41.sketch_text.stroke-0")}),-1.0]])]});
            var Q9;
            Q9=makeQuery(id+"F11.imprint","IMPRINT",FACE,{"disambiguationData":[TD([[makeQuery(id+"F11.imprint","IMPRINT",EDGE,{"derivedFrom":sQuery(id+"F11.wireOp",EDGE,"E42.sketch_text.stroke-0")}),-1.0]])]});
            var Q10;
            Q10=makeQuery(id+"F11.imprint","IMPRINT",FACE,{"disambiguationData":[TD([[makeQuery(id+"F11.imprint","IMPRINT",EDGE,{"derivedFrom":sQuery(id+"F11.wireOp",EDGE,"E43.sketch_text.stroke-0")}),-1.0]])]});
            var Q11;
            {var subQ5=sQuery(id+"F11.wireOp",EDGE,"E44.sketch_text.stroke-0");Q11=makeQuery(id+"F11.imprint","IMPRINT",FACE,{"disambiguationData":[TD([[makeQuery(id+"F11.imprint","IMPRINT",EDGE,{"derivedFrom":subQ5}),-1.0]])]});}
            var Q12;
            Q12=makeQuery(id+"F11.imprint","IMPRINT",FACE,{"disambiguationData":[TD([[makeQuery(id+"F11.imprint","IMPRINT",EDGE,{"derivedFrom":sQuery(id+"F11.wireOp",EDGE,"E45.sketch_text.stroke-0")}),-1.0]])]});
            var Q13;
            {var subQ5=sQuery(id+"F11.wireOp",EDGE,"E46.sketch_text.stroke-2");Q13=makeQuery(id+"F11.imprint","IMPRINT",FACE,{"disambiguationData":[TD([[makeQuery(id+"F11.imprint","IMPRINT",EDGE,{"derivedFrom":subQ5}),-1.0]])]});}
            var Q14;
            {var subQ5=sQuery(id+"F11.wireOp",EDGE,"E47.sketch_text.stroke-1");Q14=makeQuery(id+"F11.imprint","IMPRINT",FACE,{"disambiguationData":[TD([[makeQuery(id+"F11.imprint","IMPRINT",EDGE,{"derivedFrom":subQ5}),-1.0]])]});}
            var Q15;
            Q15=makeQuery(id+"F11.imprint","IMPRINT",FACE,{"disambiguationData":[TD([[makeQuery(id+"F11.imprint","IMPRINT",EDGE,{"derivedFrom":sQuery(id+"F11.wireOp",EDGE,"E48.sketch_text.stroke-0")}),-1.0]])]});
            var Q16;
            {var subQ5=sQuery(id+"F11.wireOp",EDGE,"E49.sketch_text.stroke-7");Q16=makeQuery(id+"F11.imprint","IMPRINT",FACE,{"disambiguationData":[TD([[makeQuery(id+"F11.imprint","IMPRINT",EDGE,{"derivedFrom":subQ5}),-1.0]])]});}
            var Q17;
            Q17=makeQuery(id+"F11.imprint","IMPRINT",FACE,{"disambiguationData":[TD([[makeQuery(id+"F11.imprint","IMPRINT",EDGE,{"derivedFrom":sQuery(id+"F11.wireOp",EDGE,"E49.sketch_text.stroke-0")}),-1.0]])]});
            var Q18;
            Q18=makeQuery(id+"F11.imprint","IMPRINT",FACE,{"disambiguationData":[TD([[makeQuery(id+"F11.imprint","IMPRINT",EDGE,{"derivedFrom":sQuery(id+"F11.wireOp",EDGE,"E50.sketch_text.stroke-0")}),-1.0]])]});
            var Q19;
            {var subQ11=sQuery(id+"F11.wireOp",EDGE,"E51.sketch_text.stroke-2");Q19=makeQuery(id+"F11.imprint","IMPRINT",FACE,{"disambiguationData":[TD([[makeQuery(id+"F11.imprint","IMPRINT",EDGE,{"derivedFrom":subQ11}),-1.0]])]});}
            var Q20;
            {var subQ6=sQuery(id+"F11.wireOp",EDGE,"E52.sketch_text.stroke-0");Q20=makeQuery(id+"F11.imprint","IMPRINT",FACE,{"disambiguationData":[TD([[makeQuery(id+"F11.imprint","IMPRINT",EDGE,{"derivedFrom":subQ6}),-1.0]])]});}
            var Q21;
            {var subQ0=sQuery(id+"F11.wireOp",EDGE,"E35.sketch_text.stroke-1");var subQ1=sQuery(id+"F11.wireOp",EDGE,"E32");var subQ2=makeQuery(id+"F11.imprint","INTERSECT",VERTEX,{"derivedFrom":[subQ1,subQ0]});Q21=makeQuery(id+"F11.imprint","IMPRINT",FACE,{"disambiguationData":[TD([[makeQuery(id+"F11.imprint","IMPRINT",EDGE,{"disambiguationData":[TD([[subQ2,-1.0]])],"derivedFrom":subQ1}),1.0]])]});}
            var Q22;
            {var subQ5=sQuery(id+"F11.wireOp",EDGE,"E36.sketch_text.stroke-10");Q22=makeQuery(id+"F11.imprint","IMPRINT",FACE,{"disambiguationData":[TD([[makeQuery(id+"F11.imprint","IMPRINT",EDGE,{"derivedFrom":subQ5}),-1.0]])]});}
            var Q23;
            {var subQ5=sQuery(id+"F11.wireOp",EDGE,"E33.sketch_text.stroke-3");Q23=makeQuery(id+"F11.imprint","IMPRINT",FACE,{"disambiguationData":[TD([[makeQuery(id+"F11.imprint","IMPRINT",EDGE,{"derivedFrom":subQ5}),-1.0]])]});}
            var Q24;
            {var subQ0=sQuery(id+"F11.wireOp",EDGE,"E37.sketch_text.stroke-3");Q24=makeQuery(id+"F11.imprint","IMPRINT",FACE,{"disambiguationData":[TD([[makeQuery(id+"F11.imprint","IMPRINT",EDGE,{"derivedFrom":subQ0}),-1.0]])]});}
            var Q25;
            {var subQ5=sQuery(id+"F11.wireOp",EDGE,"E37.sketch_text.stroke-7");Q25=makeQuery(id+"F11.imprint","IMPRINT",FACE,{"disambiguationData":[TD([[makeQuery(id+"F11.imprint","IMPRINT",EDGE,{"derivedFrom":subQ5}),-1.0]])]});}
            var Q26;
            {var subQ5=sQuery(id+"F11.wireOp",EDGE,"E38.sketch_text.stroke-5");Q26=makeQuery(id+"F11.imprint","IMPRINT",FACE,{"disambiguationData":[TD([[makeQuery(id+"F11.imprint","IMPRINT",EDGE,{"derivedFrom":subQ5}),-1.0]])]});}
            var Q27;
            {var subQ5=sQuery(id+"F11.wireOp",EDGE,"E39.sketch_text.stroke-5");Q27=makeQuery(id+"F11.imprint","IMPRINT",FACE,{"disambiguationData":[TD([[makeQuery(id+"F11.imprint","IMPRINT",EDGE,{"derivedFrom":subQ5}),-1.0]])]});}
            var Q28;
            {var subQ5=sQuery(id+"F11.wireOp",EDGE,"E40.sketch_text.stroke-3");Q28=makeQuery(id+"F11.imprint","IMPRINT",FACE,{"disambiguationData":[TD([[makeQuery(id+"F11.imprint","IMPRINT",EDGE,{"derivedFrom":subQ5}),-1.0]])]});}
            var Q29;
            {var subQ5=sQuery(id+"F11.wireOp",EDGE,"E40.sketch_text.stroke-17");Q29=makeQuery(id+"F11.imprint","IMPRINT",FACE,{"disambiguationData":[TD([[makeQuery(id+"F11.imprint","IMPRINT",EDGE,{"derivedFrom":subQ5}),-1.0]])]});}
            var Q30;
            {var subQ0=sQuery(id+"F11.wireOp",EDGE,"E41.sketch_text.stroke-4");var subQ1=sQuery(id+"F11.wireOp",EDGE,"E32");var subQ2=makeQuery(id+"F11.imprint","INTERSECT",VERTEX,{"derivedFrom":[subQ1,subQ0]});Q30=makeQuery(id+"F11.imprint","IMPRINT",FACE,{"disambiguationData":[TD([[makeQuery(id+"F11.imprint","IMPRINT",EDGE,{"disambiguationData":[TD([[subQ2,1.0]])],"derivedFrom":subQ1}),1.0]])]});}
            var Q31;
            {var subQ5=sQuery(id+"F11.wireOp",EDGE,"E41.sketch_text.stroke-7");Q31=makeQuery(id+"F11.imprint","IMPRINT",FACE,{"disambiguationData":[TD([[makeQuery(id+"F11.imprint","IMPRINT",EDGE,{"derivedFrom":subQ5}),-1.0]])]});}
            var Q32;
            {var subQ0=sQuery(id+"F11.wireOp",EDGE,"E42.sketch_text.stroke-9");var subQ1=sQuery(id+"F11.wireOp",EDGE,"E32");var subQ2=makeQuery(id+"F11.imprint","INTERSECT",VERTEX,{"derivedFrom":[subQ1,subQ0]});Q32=makeQuery(id+"F11.imprint","IMPRINT",FACE,{"disambiguationData":[TD([[makeQuery(id+"F11.imprint","IMPRINT",EDGE,{"disambiguationData":[TD([[subQ2,-1.0]])],"derivedFrom":subQ1}),1.0]])]});}
            var Q33;
            {var subQ5=sQuery(id+"F11.wireOp",EDGE,"E43.sketch_text.stroke-6");Q33=makeQuery(id+"F11.imprint","IMPRINT",FACE,{"disambiguationData":[TD([[makeQuery(id+"F11.imprint","IMPRINT",EDGE,{"derivedFrom":subQ5}),-1.0]])]});}
            var Q34;
            {var subQ0=sQuery(id+"F11.wireOp",EDGE,"E44.sketch_text.stroke-1");var subQ1=sQuery(id+"F11.wireOp",EDGE,"E32");var subQ2=makeQuery(id+"F11.imprint","INTERSECT",VERTEX,{"derivedFrom":[subQ1,subQ0]});Q34=makeQuery(id+"F11.imprint","IMPRINT",FACE,{"disambiguationData":[TD([[makeQuery(id+"F11.imprint","IMPRINT",EDGE,{"disambiguationData":[TD([[subQ2,-1.0]])],"derivedFrom":subQ1}),1.0]])]});}
            var Q35;
            {var subQ0=sQuery(id+"F11.wireOp",EDGE,"E45.sketch_text.stroke-9");var subQ1=sQuery(id+"F11.wireOp",EDGE,"E32");var subQ2=makeQuery(id+"F11.imprint","INTERSECT",VERTEX,{"derivedFrom":[subQ1,subQ0]});Q35=makeQuery(id+"F11.imprint","IMPRINT",FACE,{"disambiguationData":[TD([[makeQuery(id+"F11.imprint","IMPRINT",EDGE,{"disambiguationData":[TD([[subQ2,-1.0]])],"derivedFrom":subQ1}),1.0]])]});}
            var Q36;
            {var subQ5=sQuery(id+"F11.wireOp",EDGE,"E47.sketch_text.stroke-3");Q36=makeQuery(id+"F11.imprint","IMPRINT",FACE,{"disambiguationData":[TD([[makeQuery(id+"F11.imprint","IMPRINT",EDGE,{"derivedFrom":subQ5}),-1.0]])]});}
            var Q37;
            {var subQ5=sQuery(id+"F11.wireOp",EDGE,"E47.sketch_text.stroke-16");Q37=makeQuery(id+"F11.imprint","IMPRINT",FACE,{"disambiguationData":[TD([[makeQuery(id+"F11.imprint","IMPRINT",EDGE,{"derivedFrom":subQ5}),-1.0]])]});}
            var Q38;
            {var subQ0=sQuery(id+"F11.wireOp",EDGE,"E48.sketch_text.stroke-2");var subQ1=sQuery(id+"F11.wireOp",EDGE,"E32");var subQ2=makeQuery(id+"F11.imprint","INTERSECT",VERTEX,{"derivedFrom":[subQ1,subQ0]});Q38=makeQuery(id+"F11.imprint","IMPRINT",FACE,{"disambiguationData":[TD([[makeQuery(id+"F11.imprint","IMPRINT",EDGE,{"disambiguationData":[TD([[subQ2,-1.0]])],"derivedFrom":subQ1}),1.0]])]});}
            var Q39;
            {var subQ0=sQuery(id+"F11.wireOp",EDGE,"E50.sketch_text.stroke-9");var subQ1=sQuery(id+"F11.wireOp",EDGE,"E32");var subQ2=makeQuery(id+"F11.imprint","INTERSECT",VERTEX,{"derivedFrom":[subQ1,subQ0]});Q39=makeQuery(id+"F11.imprint","IMPRINT",FACE,{"disambiguationData":[TD([[makeQuery(id+"F11.imprint","IMPRINT",EDGE,{"disambiguationData":[TD([[subQ2,-1.0]])],"derivedFrom":subQ1}),1.0]])]});}
            var Q40;
            {var subQ5=sQuery(id+"F11.wireOp",EDGE,"E51.sketch_text.stroke-7");Q40=makeQuery(id+"F11.imprint","IMPRINT",FACE,{"disambiguationData":[TD([[makeQuery(id+"F11.imprint","IMPRINT",EDGE,{"derivedFrom":subQ5}),-1.0]])]});}
            var Q41;
            {var subQ5=sQuery(id+"F11.wireOp",EDGE,"E51.sketch_text.stroke-0");Q41=makeQuery(id+"F11.imprint","IMPRINT",FACE,{"disambiguationData":[TD([[makeQuery(id+"F11.imprint","IMPRINT",EDGE,{"derivedFrom":subQ5}),-1.0]])]});}
            var Q42;
            {var subQ5=sQuery(id+"F11.wireOp",EDGE,"E52.sketch_text.stroke-2");Q42=makeQuery(id+"F11.imprint","IMPRINT",FACE,{"disambiguationData":[TD([[makeQuery(id+"F11.imprint","IMPRINT",EDGE,{"derivedFrom":subQ5}),-1.0]])]});}
            extrude(context, id + "F12", {"entities" : qUnion([Q0, Q1, Q2, Q3, Q4, Q5, Q6, Q7, Q8, Q9, Q10, Q11, Q12, Q13, Q14, Q15, Q16, Q17, Q18, Q19, Q20, Q21, Q22, Q23, Q24, Q25, Q26, Q27, Q28, Q29, Q30, Q31, Q32, Q33, Q34, Q35, Q36, Q37, Q38, Q39, Q40, Q41, Q42]), "operationType" : NewBodyOperationType.REMOVE, "oppositeDirection" : true, "depth" : 1 * mm, "offsetDistance" : 25 * mm});
        }
        {
            var Q0;
            Q0=makeQuery(id+"F1.opExtrude","CAP_FACE",FACE,{"disambiguationData":[OSD([sQuery(id+"F0.wireOp",EDGE,"E0"),sQuery(id+"F0.wireOp",EDGE,"E4"),sQuery(id+"F0.wireOp",EDGE,"E6.MirrorCS"),sQuery(id+"F0.wireOp",EDGE,"E8.MirrorCS"),sQuery(id+"F0.wireOp",EDGE,"E9.MirrorCS"),sQuery(id+"F0.wireOp",EDGE,"E12.MirrorCS"),sQuery(id+"F0.wireOp",EDGE,"E13.MirrorCS"),sQuery(id+"F0.wireOp",EDGE,"E16"),sQuery(id+"F0.wireOp",EDGE,"E17.trimOffspring"),sQuery(id+"F0.wireOp",EDGE,"E18.trimOffspring")])],"isStart":true});
            var sketch = newSketch(context, id + "F13", { "sketchPlane" : qUnion([Q0])});
            skCircle(sketch, "E53", {"center": v(0, 0.05) * mm, "radius": 11 * mm});
            skCircle(sketch, "E54", {"center": v(0, 0.05) * mm, "radius": 16 * mm});
            skText(sketch, "E55", { "text": "6", "fontName": "OpenSans-Bold.ttf"});
            skText(sketch, "E56", { "text": "7", "fontName": "OpenSans-Bold.ttf"});
            skText(sketch, "E57", { "text": "8", "fontName": "OpenSans-Bold.ttf"});
            skText(sketch, "E58", { "text": "-", "fontName": "OpenSans-Bold.ttf"});
            skText(sketch, "E59", { "text": "9", "fontName": "OpenSans-Bold.ttf"});
            skText(sketch, "E60", { "text": "9", "fontName": "OpenSans-Bold.ttf"});
            skText(sketch, "E61", { "text": "9", "fontName": "OpenSans-Bold.ttf"});
            skText(sketch, "E62", { "text": "-", "fontName": "OpenSans-Bold.ttf"});
            skText(sketch, "E63", { "text": "7", "fontName": "OpenSans-Bold.ttf"});
            skText(sketch, "E64", { "text": "5", "fontName": "OpenSans-Bold.ttf"});
            skText(sketch, "E65", { "text": "4", "fontName": "OpenSans-Bold.ttf"});
            skText(sketch, "E66", { "text": "1", "fontName": "OpenSans-Bold.ttf"});
            const initialGuessF13  = {"E55": [0.01561, 0.00357, 0.0378, -0.99929, 0.007], "E56": [0.01593, -0.0015, -0.27759, -0.9607, 0.007], "E57": [0.01462, -0.00648, -0.56751, -0.82336, 0.007], "E58": [0.0114, -0.01118, -0.77471, -0.63231, 0.007], "E59": [0.00856, -0.01348, -0.92858, -0.37112, 0.007], "E60": [-0.00296, -0.01568, -0.93243, 0.36136, 0.007], "E61": [0.00293, -0.01568, -1, -0.00048, 0.007], "E62": [-0.00848, -0.01352, -0.78527, 0.61915, 0.007], "E63": [-0.01114, -0.01143, -0.5772, 0.8166, 0.007], "E64": [-0.01418, -0.00735, -0.2955, 0.95534, 0.007], "E65": [-0.01583, -0.00224, 0.04623, 0.99893, 0.007], "E66": [-0.01576, 0.00278, 0.31196, 0.9501, 0.007]};
            skSetInitialGuess(sketch, initialGuessF13);
            skSolve(sketch);
        }
        {
            var Q0;
            {var subQ0=sQuery(id+"F13.wireOp",EDGE,"E66.sketch_text.stroke-2");Q0=makeQuery(id+"F13.imprint","IMPRINT",FACE,{"disambiguationData":[TD([[makeQuery(id+"F13.imprint","IMPRINT",EDGE,{"derivedFrom":subQ0}),-1.0]])]});}
            var Q1;
            {var subQ2=sQuery(id+"F13.wireOp",EDGE,"E65.sketch_text.stroke-0");Q1=makeQuery(id+"F13.imprint","IMPRINT",FACE,{"disambiguationData":[TD([[makeQuery(id+"F13.imprint","IMPRINT",EDGE,{"derivedFrom":subQ2}),-1.0]])]});}
            var Q2;
            Q2=makeQuery(id+"F13.imprint","IMPRINT",FACE,{"disambiguationData":[TD([[makeQuery(id+"F13.imprint","IMPRINT",EDGE,{"derivedFrom":sQuery(id+"F13.wireOp",EDGE,"E64.sketch_text.stroke-0")}),-1.0]])]});
            var Q3;
            {var subQ0=sQuery(id+"F13.wireOp",EDGE,"E63.sketch_text.stroke-1");Q3=makeQuery(id+"F13.imprint","IMPRINT",FACE,{"disambiguationData":[TD([[makeQuery(id+"F13.imprint","IMPRINT",EDGE,{"derivedFrom":subQ0}),-1.0]])]});}
            var Q4;
            Q4=makeQuery(id+"F13.imprint","IMPRINT",FACE,{"disambiguationData":[TD([[makeQuery(id+"F13.imprint","IMPRINT",EDGE,{"derivedFrom":sQuery(id+"F13.wireOp",EDGE,"E55.sketch_text.stroke-0")}),-1.0]])]});
            var Q5;
            {var subQ5=sQuery(id+"F13.wireOp",EDGE,"E56.sketch_text.stroke-1");Q5=makeQuery(id+"F13.imprint","IMPRINT",FACE,{"disambiguationData":[TD([[makeQuery(id+"F13.imprint","IMPRINT",EDGE,{"derivedFrom":subQ5}),-1.0]])]});}
            var Q6;
            Q6=makeQuery(id+"F13.imprint","IMPRINT",FACE,{"disambiguationData":[TD([[makeQuery(id+"F13.imprint","IMPRINT",EDGE,{"derivedFrom":sQuery(id+"F13.wireOp",EDGE,"E57.sketch_text.stroke-0")}),-1.0]])]});
            var Q7;
            Q7=makeQuery(id+"F13.imprint","IMPRINT",FACE,{"disambiguationData":[TD([[makeQuery(id+"F13.imprint","IMPRINT",EDGE,{"derivedFrom":sQuery(id+"F13.wireOp",EDGE,"E62.sketch_text.stroke-0")}),-1.0]])]});
            var Q8;
            Q8=makeQuery(id+"F13.imprint","IMPRINT",FACE,{"disambiguationData":[TD([[makeQuery(id+"F13.imprint","IMPRINT",EDGE,{"derivedFrom":sQuery(id+"F13.wireOp",EDGE,"E58.sketch_text.stroke-0")}),-1.0]])]});
            var Q9;
            {var subQ5=sQuery(id+"F13.wireOp",EDGE,"E59.sketch_text.stroke-0");Q9=makeQuery(id+"F13.imprint","IMPRINT",FACE,{"disambiguationData":[TD([[makeQuery(id+"F13.imprint","IMPRINT",EDGE,{"derivedFrom":subQ5}),-1.0]])]});}
            var Q10;
            {var subQ1=sQuery(id+"F13.wireOp",EDGE,"E61.sketch_text.stroke-0");Q10=makeQuery(id+"F13.imprint","IMPRINT",FACE,{"disambiguationData":[TD([[makeQuery(id+"F13.imprint","IMPRINT",EDGE,{"derivedFrom":subQ1}),-1.0]])]});}
            var Q11;
            {var subQ1=sQuery(id+"F13.wireOp",EDGE,"E60.sketch_text.stroke-0");Q11=makeQuery(id+"F13.imprint","IMPRINT",FACE,{"disambiguationData":[TD([[makeQuery(id+"F13.imprint","IMPRINT",EDGE,{"derivedFrom":subQ1}),-1.0]])]});}
            var Q12;
            {var subQ5=sQuery(id+"F13.wireOp",EDGE,"E60.sketch_text.stroke-2");Q12=makeQuery(id+"F13.imprint","IMPRINT",FACE,{"disambiguationData":[TD([[makeQuery(id+"F13.imprint","IMPRINT",EDGE,{"derivedFrom":subQ5}),-1.0]])]});}
            var Q13;
            {var subQ5=sQuery(id+"F13.wireOp",EDGE,"E61.sketch_text.stroke-2");Q13=makeQuery(id+"F13.imprint","IMPRINT",FACE,{"disambiguationData":[TD([[makeQuery(id+"F13.imprint","IMPRINT",EDGE,{"derivedFrom":subQ5}),-1.0]])]});}
            var Q14;
            {var subQ5=sQuery(id+"F13.wireOp",EDGE,"E63.sketch_text.stroke-6");Q14=makeQuery(id+"F13.imprint","IMPRINT",FACE,{"disambiguationData":[TD([[makeQuery(id+"F13.imprint","IMPRINT",EDGE,{"derivedFrom":subQ5}),-1.0]])]});}
            var Q15;
            {var subQ0=sQuery(id+"F13.wireOp",EDGE,"E64.sketch_text.stroke-3");var subQ1=sQuery(id+"F13.wireOp",EDGE,"E54");var subQ2=makeQuery(id+"F13.imprint","INTERSECT",VERTEX,{"derivedFrom":[subQ1,subQ0]});Q15=makeQuery(id+"F13.imprint","IMPRINT",FACE,{"disambiguationData":[TD([[makeQuery(id+"F13.imprint","IMPRINT",EDGE,{"disambiguationData":[TD([[subQ2,-1.0]])],"derivedFrom":subQ1}),1.0]])]});}
            var Q16;
            {var subQ5=sQuery(id+"F13.wireOp",EDGE,"E65.sketch_text.stroke-2");Q16=makeQuery(id+"F13.imprint","IMPRINT",FACE,{"disambiguationData":[TD([[makeQuery(id+"F13.imprint","IMPRINT",EDGE,{"derivedFrom":subQ5}),-1.0]])]});}
            var Q17;
            {var subQ5=sQuery(id+"F13.wireOp",EDGE,"E66.sketch_text.stroke-0");Q17=makeQuery(id+"F13.imprint","IMPRINT",FACE,{"disambiguationData":[TD([[makeQuery(id+"F13.imprint","IMPRINT",EDGE,{"derivedFrom":subQ5}),-1.0]])]});}
            var Q18;
            {var subQ5=sQuery(id+"F13.wireOp",EDGE,"E59.sketch_text.stroke-2");Q18=makeQuery(id+"F13.imprint","IMPRINT",FACE,{"disambiguationData":[TD([[makeQuery(id+"F13.imprint","IMPRINT",EDGE,{"derivedFrom":subQ5}),-1.0]])]});}
            var Q19;
            {var subQ0=sQuery(id+"F13.wireOp",EDGE,"E57.sketch_text.stroke-7");var subQ1=sQuery(id+"F13.wireOp",EDGE,"E54");var subQ2=makeQuery(id+"F13.imprint","INTERSECT",VERTEX,{"derivedFrom":[subQ1,subQ0]});Q19=makeQuery(id+"F13.imprint","IMPRINT",FACE,{"disambiguationData":[TD([[makeQuery(id+"F13.imprint","IMPRINT",EDGE,{"disambiguationData":[TD([[subQ2,-1.0]])],"derivedFrom":subQ1}),1.0]])]});}
            var Q20;
            {var subQ5=sQuery(id+"F13.wireOp",EDGE,"E56.sketch_text.stroke-6");Q20=makeQuery(id+"F13.imprint","IMPRINT",FACE,{"disambiguationData":[TD([[makeQuery(id+"F13.imprint","IMPRINT",EDGE,{"derivedFrom":subQ5}),-1.0]])]});}
            var Q21;
            {var subQ0=sQuery(id+"F13.wireOp",EDGE,"E55.sketch_text.stroke-14");var subQ1=sQuery(id+"F13.wireOp",EDGE,"E54");var subQ2=makeQuery(id+"F13.imprint","INTERSECT",VERTEX,{"derivedFrom":[subQ1,subQ0]});Q21=makeQuery(id+"F13.imprint","IMPRINT",FACE,{"disambiguationData":[TD([[makeQuery(id+"F13.imprint","IMPRINT",EDGE,{"disambiguationData":[TD([[subQ2,1.0]])],"derivedFrom":subQ1}),1.0]])]});}
            extrude(context, id + "F14", {"entities" : qUnion([Q0, Q1, Q2, Q3, Q4, Q5, Q6, Q7, Q8, Q9, Q10, Q11, Q12, Q13, Q14, Q15, Q16, Q17, Q18, Q19, Q20, Q21]), "operationType" : NewBodyOperationType.REMOVE, "oppositeDirection" : true, "depth" : 1 * mm, "offsetDistance" : 25 * mm});
        }
    });
